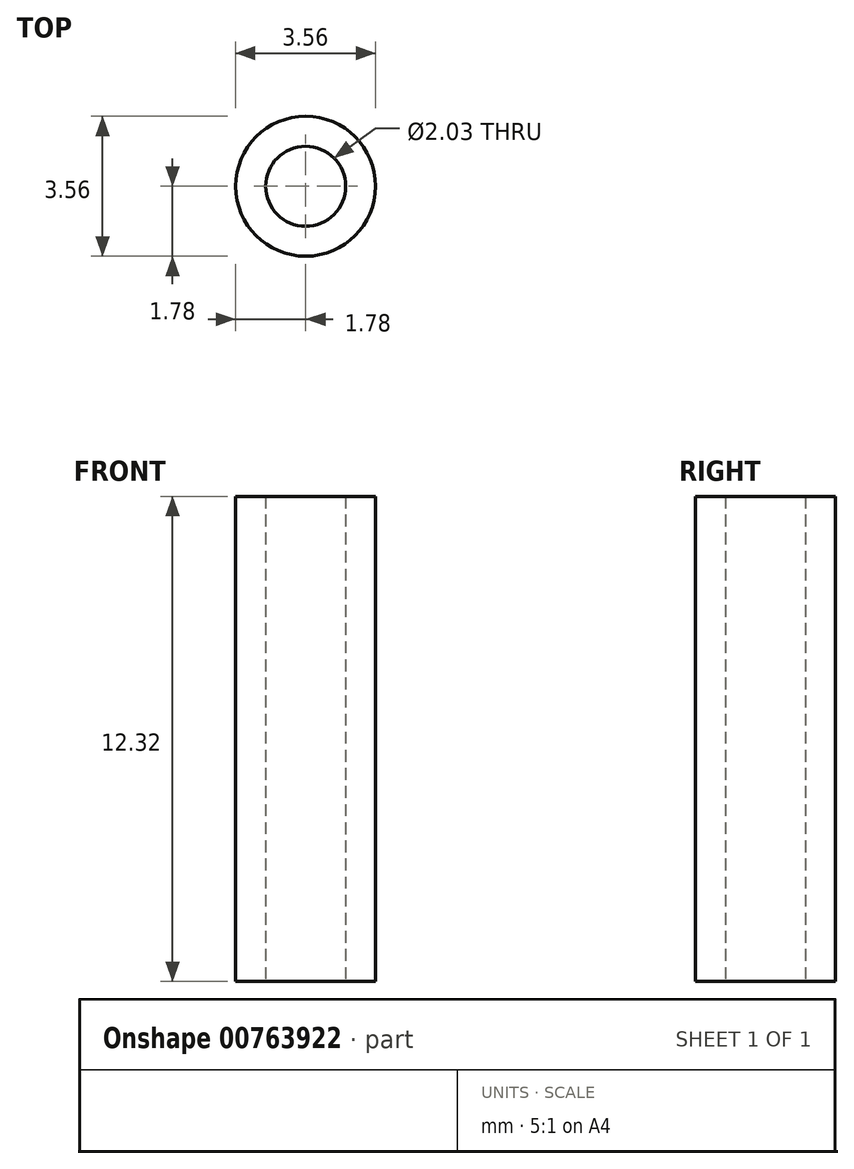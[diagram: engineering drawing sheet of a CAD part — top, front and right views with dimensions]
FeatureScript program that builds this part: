
annotation { "Feature Type Name" : "Feature", "Feature Type Description" : "" }
export const myFeature = defineFeature(function(context is Context, id is Id, definition is map)
    precondition{}
    {
        {
            var Q0;
            Q0=qCreatedBy(makeId("Top.planeOp"),FACE);
            var sketch = newSketch(context, id + "F0", { "sketchPlane" : qUnion([Q0])});
            skCircle(sketch, "E0", {"center": v(0, 0) * mm, "radius": 1.02 * mm});
            skCircle(sketch, "E1.0", {"center": v(0, 0) * mm, "radius": 1.78 * mm});
            skSolve(sketch);
        }
        {
            var Q0;
            Q0 = qSketchRegion(id + "F0", true);
            extrude(context, id + "F1", {"entities" : qUnion([Q0]), "depth" : 12.32 * mm, "offsetDistance" : 25.4 * mm});
        }
    });
